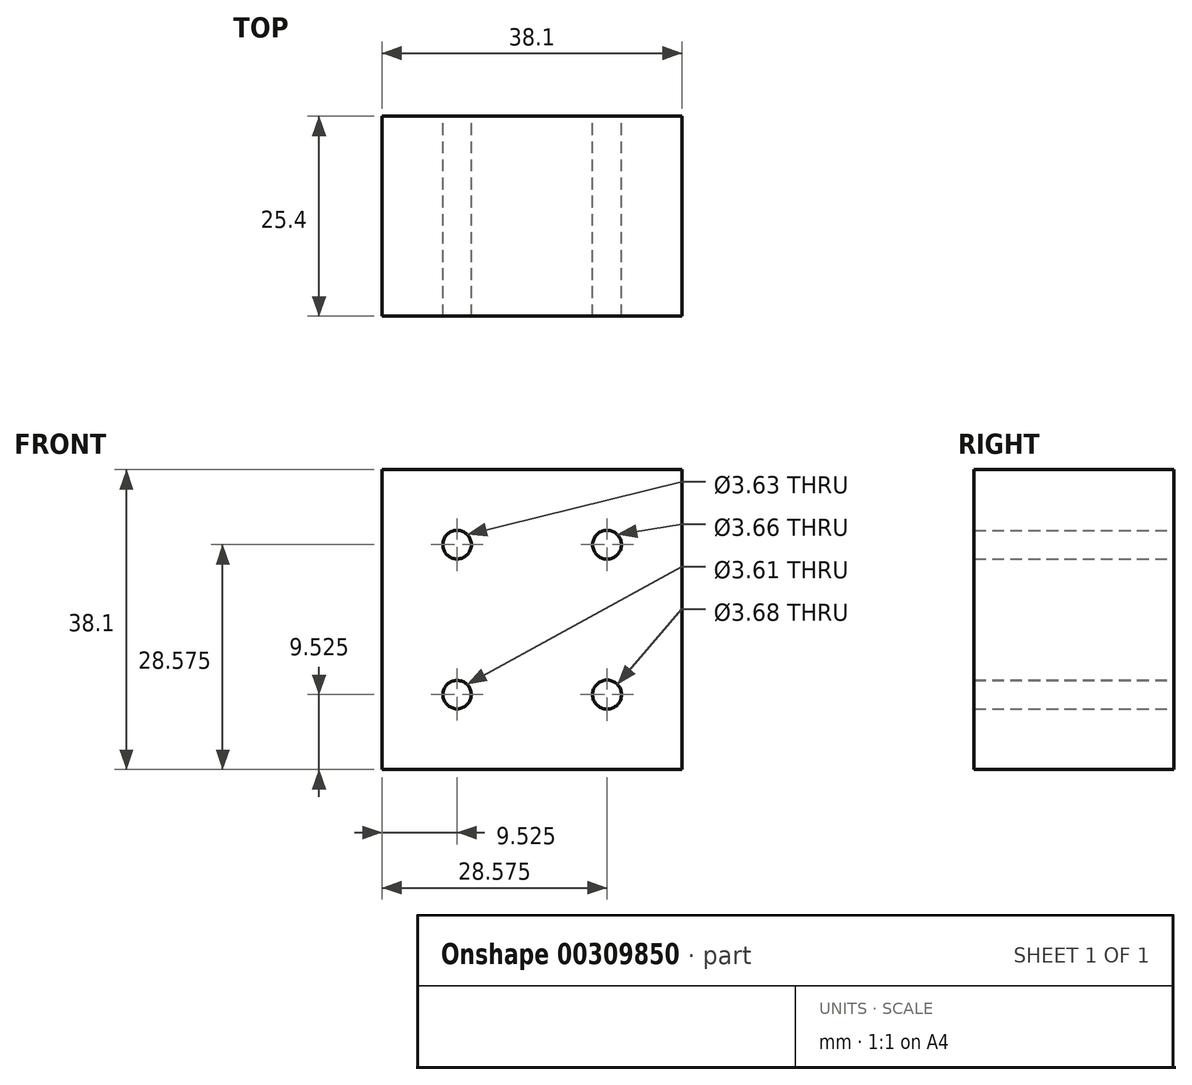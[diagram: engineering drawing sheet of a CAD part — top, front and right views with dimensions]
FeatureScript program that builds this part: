
annotation { "Feature Type Name" : "Feature", "Feature Type Description" : "" }
export const myFeature = defineFeature(function(context is Context, id is Id, definition is map)
    precondition{}
    {
        {
            var Q0;
            Q0=qCreatedBy(makeId("Front.planeOp"),FACE);
            var sketch = newSketch(context, id + "F0", { "sketchPlane" : qUnion([Q0])});
            skLineSegment(sketch, "E0.bottom", {"start": v(0, 0) * mm, "end": v(38.1, 0) * mm});
            skLineSegment(sketch, "E0.top", {"start": v(0, -38.1) * mm, "end": v(38.1, -38.1) * mm});
            skLineSegment(sketch, "E0.left", {"start": v(0, 0) * mm, "end": v(0, -38.1) * mm});
            skLineSegment(sketch, "E0.right", {"start": v(38.1, 0) * mm, "end": v(38.1, -38.1) * mm});
            skSolve(sketch);
        }
        {
            var Q0;
            Q0=qCreatedBy(makeId("Front.planeOp"),FACE);
            var sketch = newSketch(context, id + "F1", { "sketchPlane" : qUnion([Q0])});
            skLineSegment(sketch, "E1.bottom", {"start": v(0, 0) * mm, "end": v(9.53, 0) * mm});
            skLineSegment(sketch, "E1.top", {"start": v(0, -9.53) * mm, "end": v(9.53, -9.53) * mm});
            skLineSegment(sketch, "E1.left", {"start": v(0, 0) * mm, "end": v(0, -9.53) * mm});
            skLineSegment(sketch, "E1.right", {"start": v(9.53, 0) * mm, "end": v(9.53, -9.53) * mm});
            skPoint(sketch, "E2", {"position": v(9.53, -9.53) * mm});
            skPoint(sketch, "E3", {"position": v(28.58, -9.53) * mm});
            skPoint(sketch, "E4", {"position": v(9.53, -28.58) * mm});
            skPoint(sketch, "E5", {"position": v(28.57, -28.58) * mm});
            skSolve(sketch);
        }
        {
            var Q0;
            Q0=makeQuery(id+"F0.imprint","IMPRINT",FACE,{"disambiguationData":[TD([[makeQuery(id+"F0.imprint","IMPRINT",EDGE,{"derivedFrom":sQuery(id+"F0.wireOp",EDGE,"E0.bottom")}),-1.0]])]});
            extrude(context, id + "F2", {"entities" : qUnion([Q0]), "depth" : 25.4 * mm});
        }
        {
            var Q0;
            Q0=sQuery(id+"F1.wireOp",VERTEX,"E2");
            var Q1;
            Q1=makeQuery(id+"F2.opExtrude","SWEPT_BODY",BODY,{"disambiguationData":[OSD([sQuery(id+"F0.wireOp",EDGE,"E0.bottom"),sQuery(id+"F0.wireOp",EDGE,"E0.top"),sQuery(id+"F0.wireOp",EDGE,"E0.left"),sQuery(id+"F0.wireOp",EDGE,"E0.right")])]});
            hole(context, id + "F3", {"style" : HoleStyle.SIMPLE, "endStyle" : HoleEndStyle.THROUGH, "oppositeDirection" : true, "holeDiameter" : 3.63 * mm, "tappedDepth" : 12.7 * mm, "tapClearance" : 3, "locations" : qUnion([Q0]), "scope" : qUnion([Q1])});
        }
        {
            var Q0;
            Q0=sQuery(id+"F1.wireOp",VERTEX,"E3");
            var Q1;
            Q1=makeQuery(id+"F2.opExtrude","SWEPT_BODY",BODY,{"disambiguationData":[OSD([sQuery(id+"F0.wireOp",EDGE,"E0.bottom"),sQuery(id+"F0.wireOp",EDGE,"E0.top"),sQuery(id+"F0.wireOp",EDGE,"E0.left"),sQuery(id+"F0.wireOp",EDGE,"E0.right")])]});
            hole(context, id + "F4", {"style" : HoleStyle.SIMPLE, "endStyle" : HoleEndStyle.THROUGH, "oppositeDirection" : true, "holeDiameter" : 3.66 * mm, "tappedDepth" : 12.7 * mm, "tapClearance" : 3, "locations" : qUnion([Q0]), "scope" : qUnion([Q1])});
        }
        {
            var Q0;
            Q0=sQuery(id+"F1.wireOp",VERTEX,"E4");
            var Q1;
            Q1=makeQuery(id+"F2.opExtrude","SWEPT_BODY",BODY,{"disambiguationData":[OSD([sQuery(id+"F0.wireOp",EDGE,"E0.bottom"),sQuery(id+"F0.wireOp",EDGE,"E0.top"),sQuery(id+"F0.wireOp",EDGE,"E0.left"),sQuery(id+"F0.wireOp",EDGE,"E0.right")])]});
            hole(context, id + "F5", {"style" : HoleStyle.SIMPLE, "endStyle" : HoleEndStyle.THROUGH, "oppositeDirection" : true, "holeDiameter" : 3.6 * mm, "tappedDepth" : 12.7 * mm, "tapClearance" : 3, "locations" : qUnion([Q0]), "scope" : qUnion([Q1])});
        }
        {
            var Q0;
            Q0=sQuery(id+"F1.wireOp",VERTEX,"E5");
            var Q1;
            Q1=makeQuery(id+"F2.opExtrude","SWEPT_BODY",BODY,{"disambiguationData":[OSD([sQuery(id+"F0.wireOp",EDGE,"E0.bottom"),sQuery(id+"F0.wireOp",EDGE,"E0.top"),sQuery(id+"F0.wireOp",EDGE,"E0.left"),sQuery(id+"F0.wireOp",EDGE,"E0.right")])]});
            hole(context, id + "F6", {"style" : HoleStyle.SIMPLE, "endStyle" : HoleEndStyle.THROUGH, "oppositeDirection" : true, "holeDiameter" : 3.68 * mm, "tappedDepth" : 12.7 * mm, "tapClearance" : 3, "locations" : qUnion([Q0]), "scope" : qUnion([Q1])});
        }
    });
